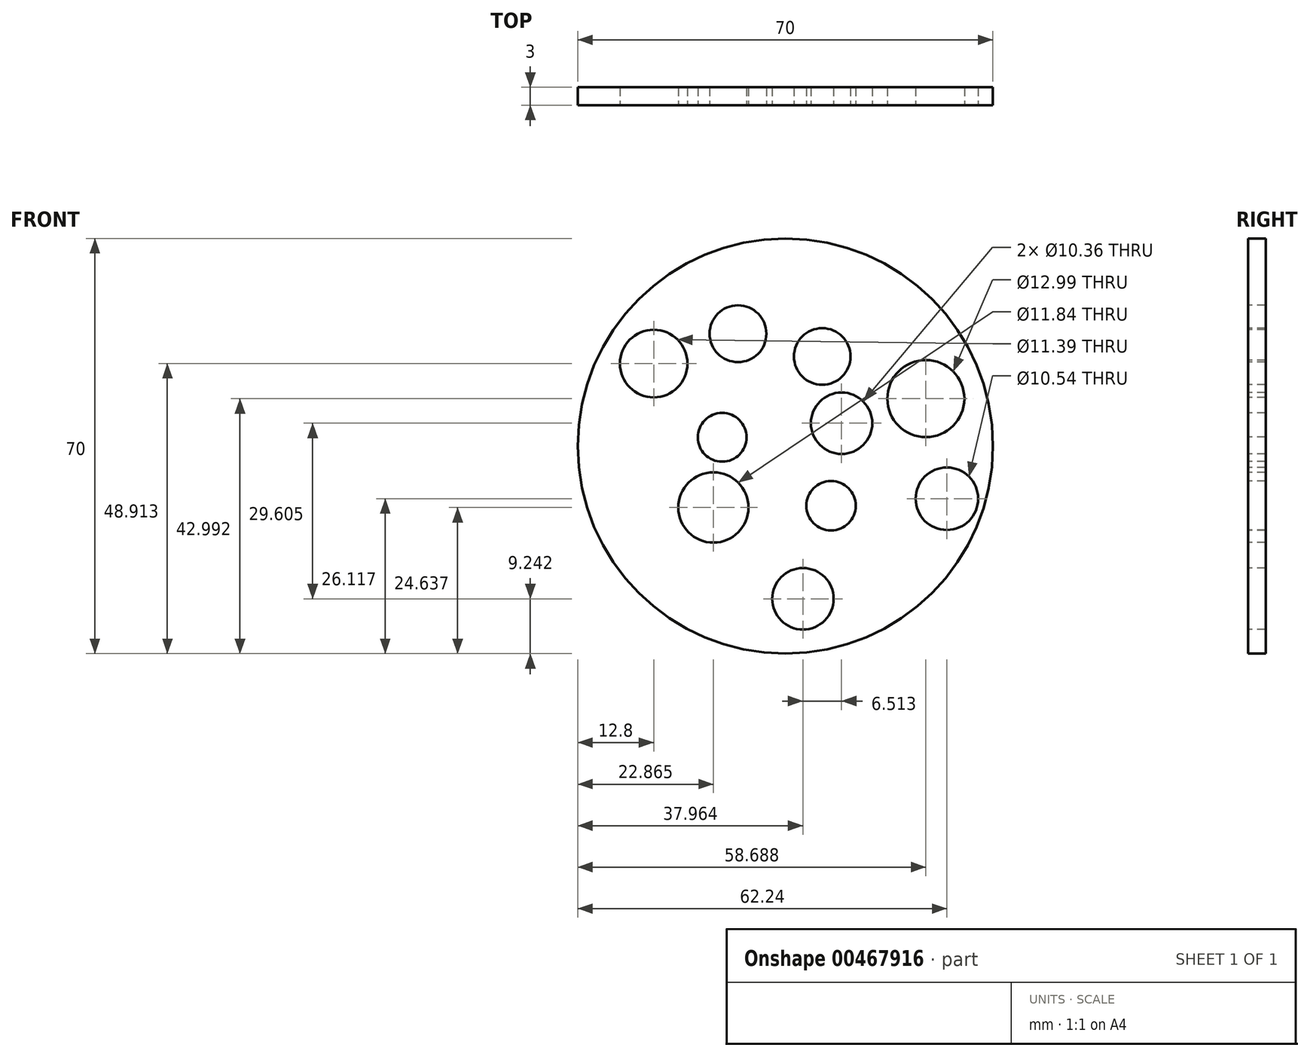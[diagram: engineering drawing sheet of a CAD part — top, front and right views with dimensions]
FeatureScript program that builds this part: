
annotation { "Feature Type Name" : "Feature", "Feature Type Description" : "" }
export const myFeature = defineFeature(function(context is Context, id is Id, definition is map)
    precondition{}
    {
        {
            var Q0;
            Q0=qCreatedBy(makeId("Front.planeOp"),FACE);
            var sketch = newSketch(context, id + "F0", { "sketchPlane" : qUnion([Q0])});
            skCircle(sketch, "E0", {"center": v(8, 16.58) * mm, "radius": 35 * mm});
            skSolve(sketch);
        }
        {
            var Q0;
            Q0=makeQuery(id+"F0.imprint","IMPRINT",FACE,{"disambiguationData":[TD([[makeQuery(id+"F0.imprint","IMPRINT",EDGE,{"derivedFrom":sQuery(id+"F0.wireOp",EDGE,"E0")}),1.0]])]});
            extrude(context, id + "F1", {"entities" : qUnion([Q0]), "depth" : 3 * mm});
        }
        {
            var Q0;
            Q0=makeQuery(id+"F1.opExtrude","CAP_FACE",FACE,{"disambiguationData":[OSD([sQuery(id+"F0.wireOp",EDGE,"E0")])],"isStart":false});
            var sketch = newSketch(context, id + "F2", { "sketchPlane" : qUnion([Q0])});
            skCircle(sketch, "E1", {"center": v(0, 35.53) * mm, "radius": 4.78 * mm});
            skCircle(sketch, "E2", {"center": v(31.68, 24.57) * mm, "radius": 6.5 * mm});
            skCircle(sketch, "E3", {"center": v(-2.66, 18.06) * mm, "radius": 4.11 * mm});
            skCircle(sketch, "E4", {"center": v(15.7, 6.51) * mm, "radius": 4.19 * mm});
            skCircle(sketch, "E5", {"center": v(14.21, 31.68) * mm, "radius": 4.77 * mm});
            skCircle(sketch, "E6", {"center": v(-4.14, 6.22) * mm, "radius": 5.92 * mm});
            skCircle(sketch, "E7", {"center": v(-14.21, 30.5) * mm, "radius": 5.7 * mm});
            skCircle(sketch, "E8", {"center": v(35.23, 7.7) * mm, "radius": 5.27 * mm});
            skCircle(sketch, "E9", {"center": v(10.95, -9.18) * mm, "radius": 5.18 * mm});
            skCircle(sketch, "E10", {"center": v(17.47, 20.43) * mm, "radius": 5.18 * mm});
            skSolve(sketch);
        }
        {
            var Q0;
            Q0 = qSketchRegion(id + "F2", true);
            extrude(context, id + "F3", {"entities" : qUnion([Q0]), "operationType" : NewBodyOperationType.REMOVE, "oppositeDirection" : true, "depth" : 25 * mm});
        }
    });
